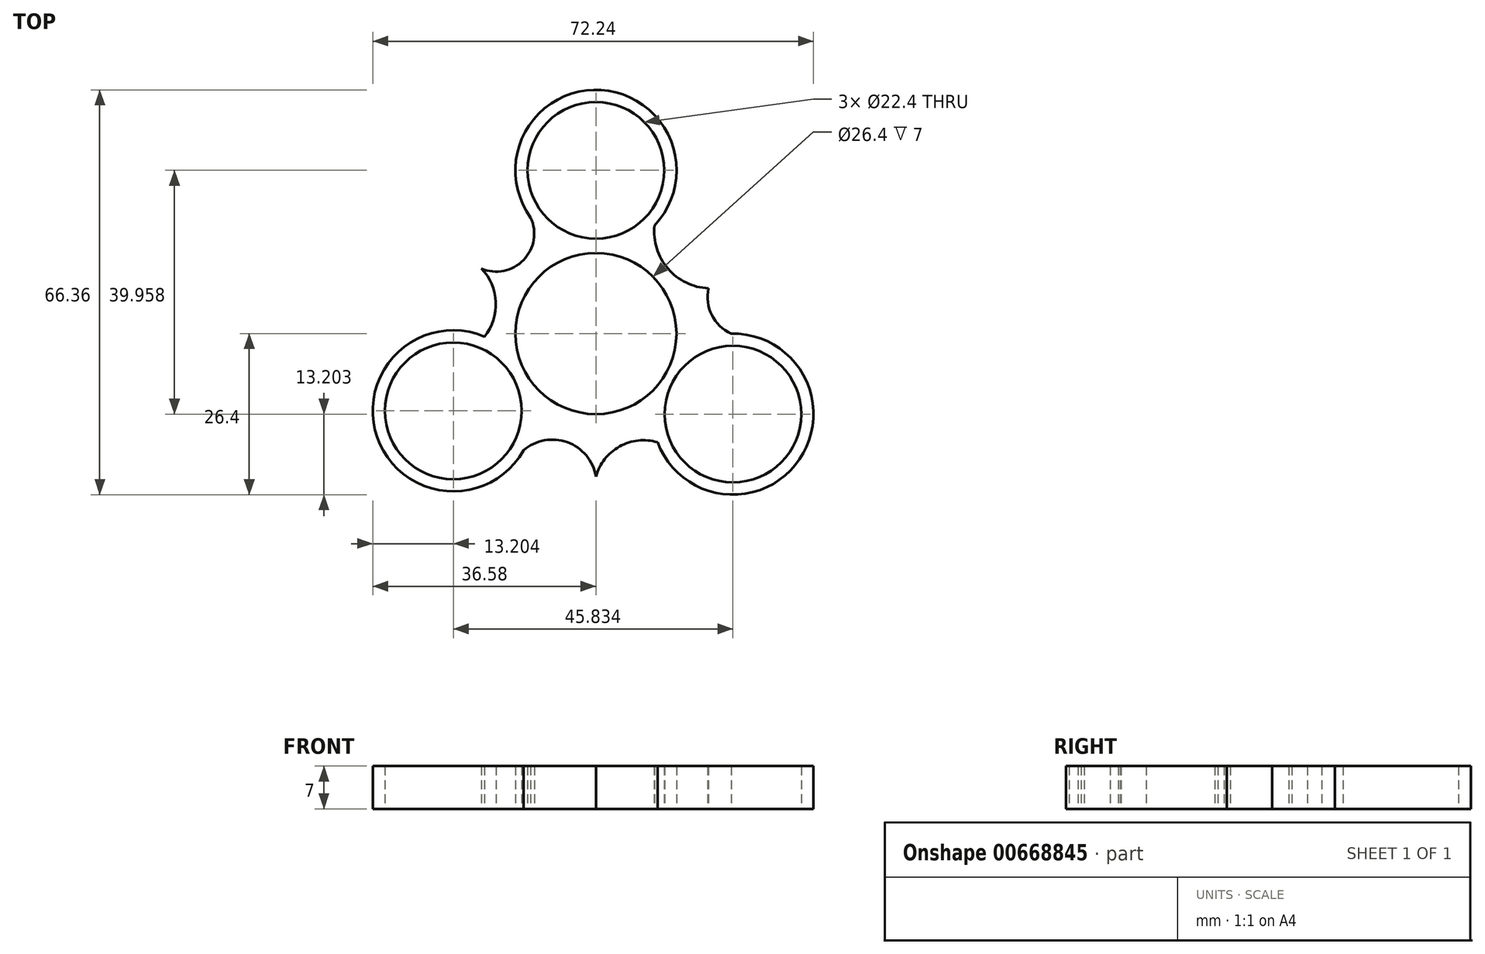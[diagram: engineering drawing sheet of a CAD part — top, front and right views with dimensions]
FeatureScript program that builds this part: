
annotation { "Feature Type Name" : "Feature", "Feature Type Description" : "" }
export const myFeature = defineFeature(function(context is Context, id is Id, definition is map)
    precondition{}
    {
        {
            var Q0;
            Q0=qCreatedBy(makeId("Top.planeOp"),FACE);
            var sketch = newSketch(context, id + "F0", { "sketchPlane" : qUnion([Q0])});
            skCircle(sketch, "E0", {"center": v(0, 0) * mm, "radius": 11.2 * mm});
            skCircle(sketch, "E1", {"center": v(0, 0) * mm, "radius": 13.2 * mm});
            skCircle(sketch, "E2", {"center": v(0, 26.76) * mm, "radius": 11.2 * mm});
            skCircle(sketch, "E3", {"center": v(0, 26.76) * mm, "radius": 13.2 * mm});
            skCircle(sketch, "E4.1.0", {"center": v(-23.38, -12.67) * mm, "radius": 13.2 * mm});
            skCircle(sketch, "E4.1.1", {"center": v(-23.38, -12.67) * mm, "radius": 11.2 * mm});
            skCircle(sketch, "E4.2.0", {"center": v(22.46, -13.2) * mm, "radius": 13.2 * mm});
            skCircle(sketch, "E4.2.1", {"center": v(22.46, -13.2) * mm, "radius": 11.2 * mm});
            skPoint(sketch, "E4.center", {"position": v(-0.3, 0.3) * mm});
            skArc(sketch, "E5", {"start": v(0, -23.41) * mm, "mid": v(-4.68, -17.81) * mm, "end": v(-11.86, -19.13) * mm});
            skArc(sketch, "E6", {"start": v(10.1, -17.81) * mm, "mid": v(3.88, -18.5) * mm, "end": v(0, -23.41) * mm});
            skPoint(sketch, "E6.startSnap0", {"position": v(-4.68, -17.81) * mm});
            skArc(sketch, "E7", {"start": v(18.45, 7.42) * mm, "mid": v(19, 3.05) * mm, "end": v(22.17, 0) * mm});
            skArc(sketch, "E8", {"start": v(9.6, 17.71) * mm, "mid": v(11.8, 10.66) * mm, "end": v(18.45, 7.42) * mm});
            skArc(sketch, "E9", {"start": v(-18.78, 10.66) * mm, "mid": v(-11.33, 12.68) * mm, "end": v(-11.56, 20.4) * mm});
            skPoint(sketch, "E9.startSnap0", {"position": v(11.8, 10.66) * mm});
            skArc(sketch, "E10", {"start": v(-18.28, -0.49) * mm, "mid": v(-16.4, 5.18) * mm, "end": v(-18.78, 10.66) * mm});
            skSolve(sketch);
        }
        {
            var Q0;
            Q0 = qSketchRegion(id + "F0", true);
            extrude(context, id + "F1", {"entities" : qUnion([Q0]), "depth" : 7 * mm, "offsetDistance" : 25 * mm});
        }
    });
